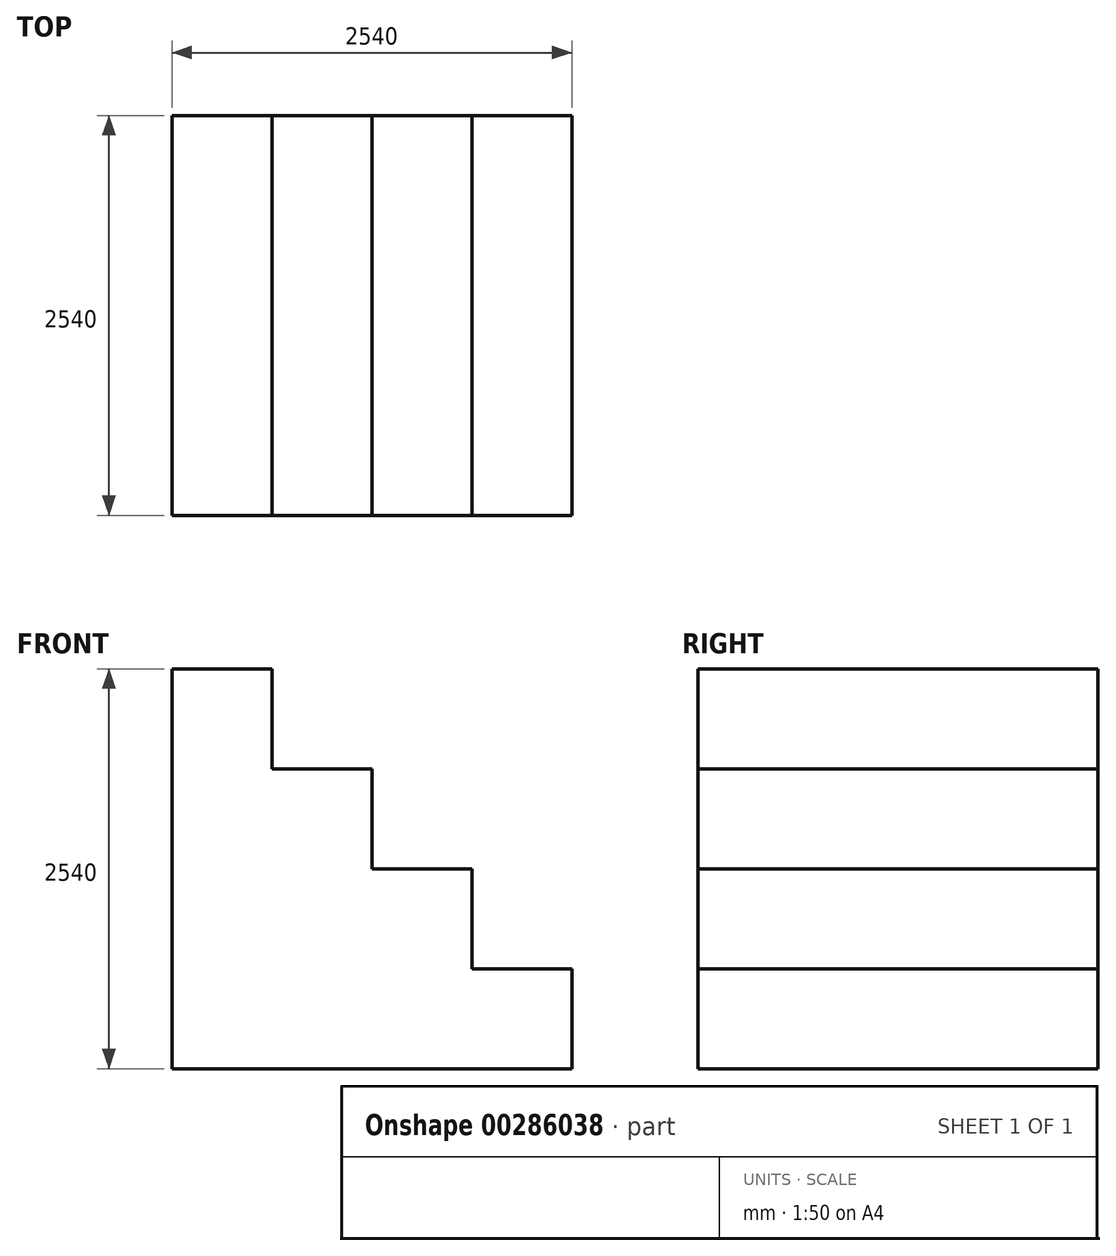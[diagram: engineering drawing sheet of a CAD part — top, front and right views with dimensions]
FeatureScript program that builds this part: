
annotation { "Feature Type Name" : "Feature", "Feature Type Description" : "" }
export const myFeature = defineFeature(function(context is Context, id is Id, definition is map)
    precondition{}
    {
        {
            var Q0;
            Q0=qCreatedBy(makeId("Front.planeOp"),FACE);
            var sketch = newSketch(context, id + "F0", { "sketchPlane" : qUnion([Q0])});
            skLineSegment(sketch, "E0", {"start": v(-950.37, 1160.51) * mm, "end": v(-950.37, -1379.49) * mm});
            skLineSegment(sketch, "E1", {"start": v(-950.37, 1160.51) * mm, "end": v(-315.37, 1160.51) * mm});
            skLineSegment(sketch, "E2", {"start": v(-315.37, 1160.51) * mm, "end": v(-315.37, 525.51) * mm});
            skLineSegment(sketch, "E3", {"start": v(-315.37, 525.51) * mm, "end": v(319.63, 525.51) * mm});
            skLineSegment(sketch, "E4", {"start": v(319.63, 525.51) * mm, "end": v(319.63, -109.49) * mm});
            skLineSegment(sketch, "E5", {"start": v(319.63, -109.49) * mm, "end": v(954.63, -109.49) * mm});
            skLineSegment(sketch, "E6", {"start": v(954.63, -109.49) * mm, "end": v(954.63, -744.49) * mm});
            skLineSegment(sketch, "E7", {"start": v(954.63, -744.49) * mm, "end": v(1589.63, -744.49) * mm});
            skLineSegment(sketch, "E8", {"start": v(1589.63, -744.49) * mm, "end": v(1589.63, -1379.49) * mm});
            skLineSegment(sketch, "E9", {"start": v(1589.63, -1379.49) * mm, "end": v(-950.37, -1379.49) * mm});
            skSolve(sketch);
        }
        {
            var Q0;
            Q0 = qSketchRegion(id + "F0", true);
            extrude(context, id + "F1", {"entities" : qUnion([Q0]), "depth" : 2540 * mm});
        }
    });
